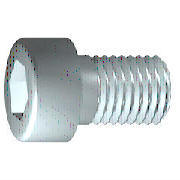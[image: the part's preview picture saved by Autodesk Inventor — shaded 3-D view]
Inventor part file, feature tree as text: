
AUTODESK INVENTOR PART (.ipt)
format: ipt  version: 2019 (Build 230136000, 136)  size: 196,096 bytes
history: native  units: mm (DEFAULTED — no unit token found)
features: sketch x3, other x1, extrude x1, plane x1, fillet x1
ambient origin geometry x7: Origin, YZ Plane, XY Plane, X Axis, Y Axis, Z Axis, Center Point
bodies: Solid1 (feature_tree)
feature tree (7):
  other  "Körper"
  extrude  "Loch"  Depth=3.0mm
  plane  "Work Plane1"
  fillet  "Fillet2"  Radius=3.0mm
  sketch  "Skizze4"  dims[d5=60.0deg d6=3.0mm d7=3.0mm d8=2.886751mm d9=5.5mm d10=90.0deg d11=10.0mm d12=0.0mm d13=10.75mm d14=0.0mm d15=0.306725mm d16=0.306725mm d17=0.3mm d19=0.0mm d26=12.0mm d27=45.0deg d28=0.0mm d29=0.0mm d30=0.1mm]
  sketch  "Skizze1"  dims[d1=10.75mm d2=0.306825mm d3=3.0mm]
  sketch  "Skizze2"  dims[d4=1.3mm]
